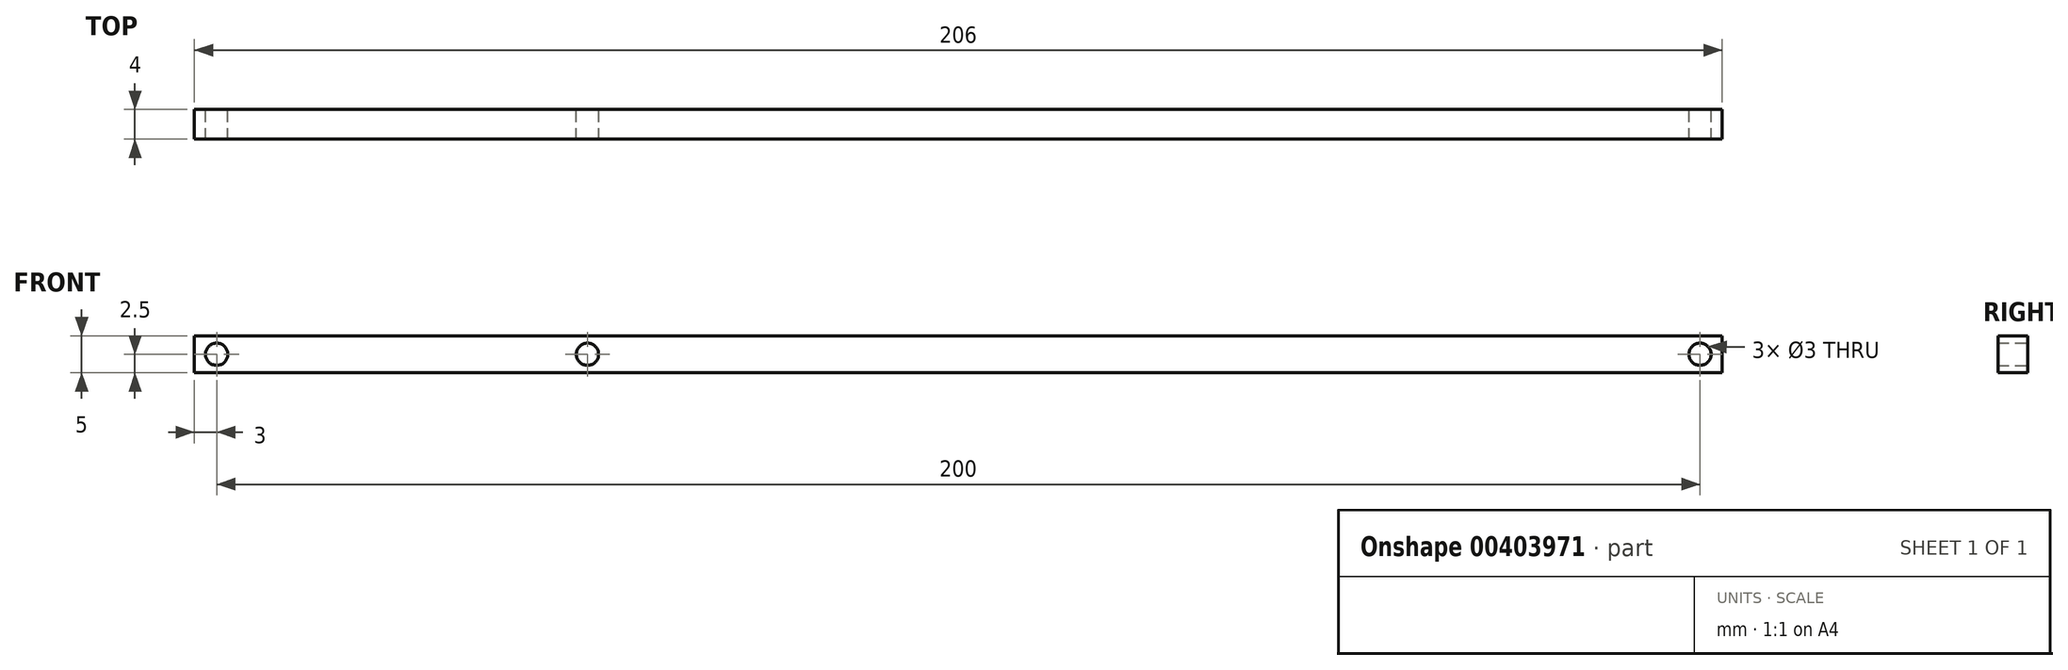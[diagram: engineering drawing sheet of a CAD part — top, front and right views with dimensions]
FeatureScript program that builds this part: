
annotation { "Feature Type Name" : "Feature", "Feature Type Description" : "" }
export const myFeature = defineFeature(function(context is Context, id is Id, definition is map)
    precondition{}
    {
        {
            var Q0;
            Q0=qCreatedBy(makeId("Front.planeOp"),FACE);
            var sketch = newSketch(context, id + "F0", { "sketchPlane" : qUnion([Q0])});
            skLineSegment(sketch, "E0.bottom", {"start": v(-143, 0) * mm, "end": v(63, 0) * mm});
            skLineSegment(sketch, "E0.top", {"start": v(-143, 5) * mm, "end": v(63, 5) * mm});
            skLineSegment(sketch, "E0.left", {"start": v(-143, 0) * mm, "end": v(-143, 5) * mm});
            skLineSegment(sketch, "E0.right", {"start": v(63, 0) * mm, "end": v(63, 5) * mm});
            skCircle(sketch, "E1", {"center": v(60, 2.5) * mm, "radius": 1.5 * mm});
            skCircle(sketch, "E2.1.0.0", {"center": v(-140, 2.5) * mm, "radius": 1.5 * mm});
            skLineSegment(sketch, "E2.direction1", {"start": v(60, 2.5) * mm, "end": v(-140, 2.5) * mm, "construction": true});
            skCircle(sketch, "E3", {"center": v(-90, 2.5) * mm, "radius": 1.5 * mm});
            skSolve(sketch);
        }
        {
            var Q0;
            Q0=makeQuery(id+"F0.imprint","IMPRINT",FACE,{"disambiguationData":[TD([[makeQuery(id+"F0.imprint","IMPRINT",EDGE,{"derivedFrom":sQuery(id+"F0.wireOp",EDGE,"E0.bottom")}),1.0]])]});
            var Q1;
            Q1=sQuery(id+"F0.wireOp",EDGE,"E0.top");
            extrude(context, id + "F1", {"entities" : qUnion([Q0]), "surfaceEntities" : qUnion([Q1]), "depth" : 4 * mm});
        }
    });
